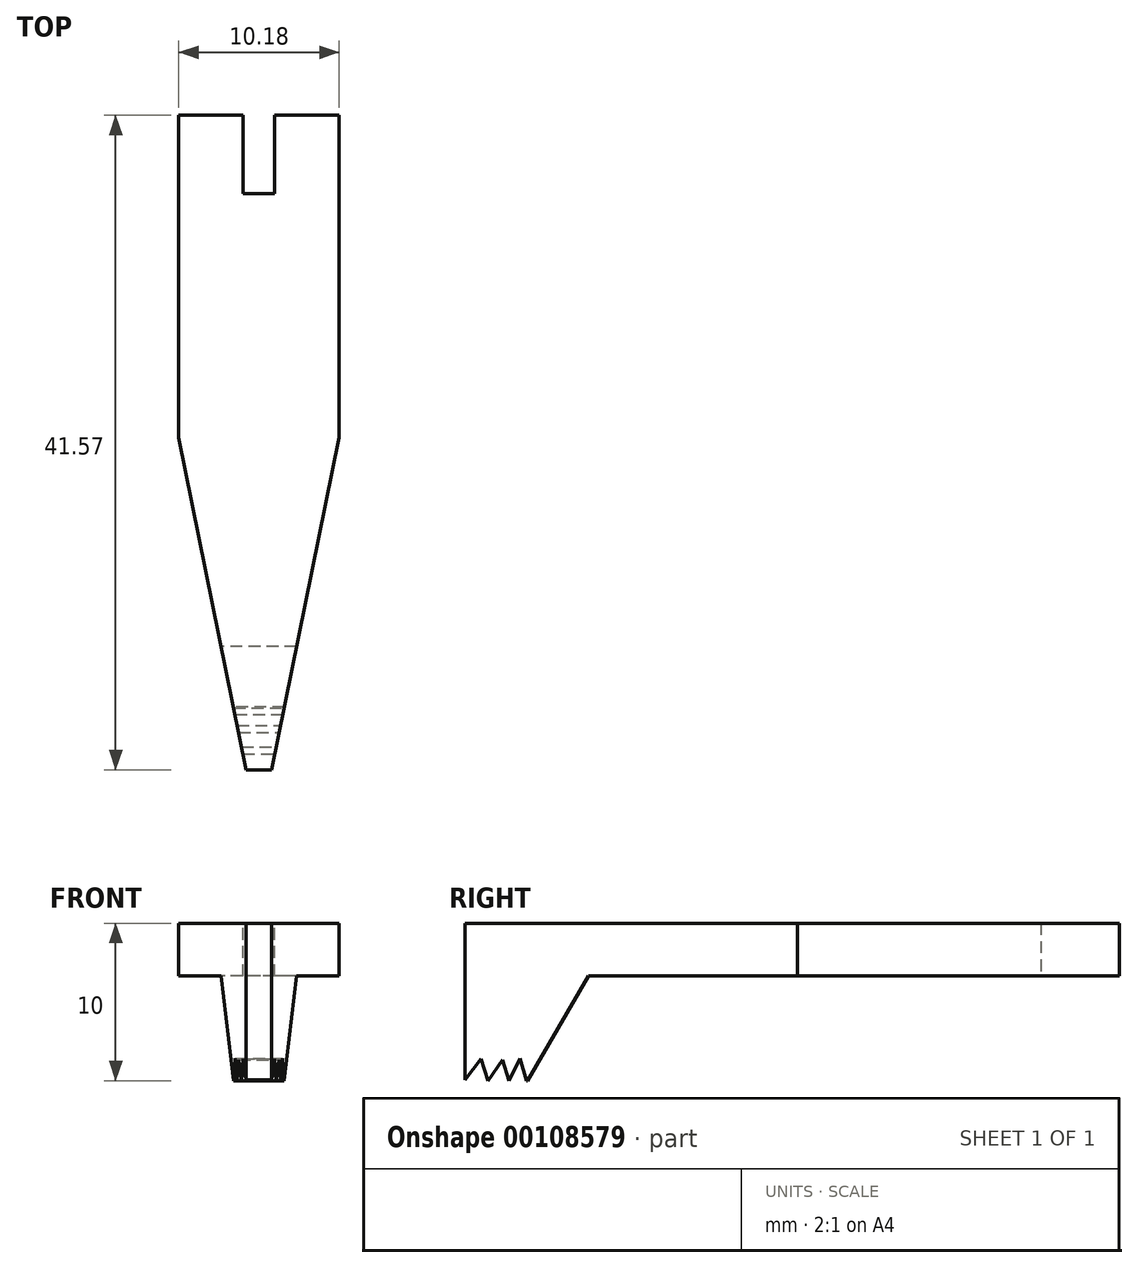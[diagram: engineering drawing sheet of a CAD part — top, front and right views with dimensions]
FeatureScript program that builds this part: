
annotation { "Feature Type Name" : "Feature", "Feature Type Description" : "" }
export const myFeature = defineFeature(function(context is Context, id is Id, definition is map)
    precondition{}
    {
        {
            var Q0;
            Q0=qCreatedBy(makeId("Top.planeOp"),FACE);
            var sketch = newSketch(context, id + "F0", { "sketchPlane" : qUnion([Q0])});
            skLineSegment(sketch, "E0", {"start": v(0, 0) * mm, "end": v(5.1, 0) * mm});
            skLineSegment(sketch, "E1", {"start": v(5.1, 0) * mm, "end": v(5.1, -20.47) * mm});
            skLineSegment(sketch, "E2", {"start": v(5.1, -20.47) * mm, "end": v(0.8, -41.57) * mm});
            skLineSegment(sketch, "E3", {"start": v(0.8, -41.57) * mm, "end": v(0, -41.57) * mm});
            skLineSegment(sketch, "E4", {"start": v(0, -41.57) * mm, "end": v(0, 0) * mm});
            skLineSegment(sketch, "E5.MirrorCS", {"start": v(0, 0) * mm, "end": v(-5.1, 0) * mm});
            skLineSegment(sketch, "E6.MirrorCS", {"start": v(-5.1, 0) * mm, "end": v(-5.1, -20.47) * mm});
            skLineSegment(sketch, "E7.MirrorCS", {"start": v(-5.1, -20.47) * mm, "end": v(-0.8, -41.57) * mm});
            skLineSegment(sketch, "E8.MirrorCS", {"start": v(-0.8, -41.57) * mm, "end": v(0, -41.57) * mm});
            skSolve(sketch);
        }
        {
            var Q0;
            Q0=makeQuery(id+"F0.imprint","IMPRINT",FACE,{"disambiguationData":[TD([[makeQuery(id+"F0.imprint","IMPRINT",EDGE,{"derivedFrom":sQuery(id+"F0.wireOp",EDGE,"E4")}),1.0]])]});
            var Q1;
            Q1=makeQuery(id+"F0.imprint","IMPRINT",FACE,{"disambiguationData":[TD([[makeQuery(id+"F0.imprint","IMPRINT",EDGE,{"derivedFrom":sQuery(id+"F0.wireOp",EDGE,"E0")}),-1.0]])]});
            extrude(context, id + "F1", {"entities" : qUnion([Q0, Q1]), "depth" : 10 * mm});
        }
        {
            var Q0;
            Q0=qCreatedBy(makeId("Right.planeOp"),FACE);
            var sketch = newSketch(context, id + "F2", { "sketchPlane" : qUnion([Q0])});
            skLineSegment(sketch, "E9", {"start": v(0, -8.96) * mm, "end": v(0, 6.65) * mm});
            skLineSegment(sketch, "E10", {"start": v(0, 6.65) * mm, "end": v(-33.74, 6.65) * mm});
            skLineSegment(sketch, "E11", {"start": v(-33.74, 6.65) * mm, "end": v(-37.6, 0) * mm});
            skLineSegment(sketch, "E12", {"start": v(-37.6, 0) * mm, "end": v(-37.6, -12.63) * mm});
            skLineSegment(sketch, "E13", {"start": v(-37.6, -12.63) * mm, "end": v(0, -8.96) * mm});
            skSolve(sketch);
        }
        {
            var Q0;
            Q0=makeQuery(id+"F2.imprint","IMPRINT",FACE,{"disambiguationData":[TD([[makeQuery(id+"F2.imprint","IMPRINT",EDGE,{"derivedFrom":sQuery(id+"F2.wireOp",EDGE,"E9")}),1.0]])]});
            extrude(context, id + "F3", {"entities" : qUnion([Q0]), "operationType" : NewBodyOperationType.REMOVE, "endBound" : BoundingType.SYMMETRIC, "depth" : 25 * mm});
        }
        {
            var Q0;
            Q0=qCreatedBy(makeId("Right.planeOp"),FACE);
            var sketch = newSketch(context, id + "F4", { "sketchPlane" : qUnion([Q0])});
            skLineSegment(sketch, "E14", {"start": v(-41.8, -0.26) * mm, "end": v(-40.56, 1.38) * mm});
            skLineSegment(sketch, "E15", {"start": v(-40.56, 1.38) * mm, "end": v(-40.1, 0) * mm});
            skLineSegment(sketch, "E16", {"start": v(-40.1, 0) * mm, "end": v(-39.2, 1.32) * mm});
            skLineSegment(sketch, "E17", {"start": v(-39.2, 1.32) * mm, "end": v(-38.77, 0) * mm});
            skLineSegment(sketch, "E18", {"start": v(-38.77, 0) * mm, "end": v(-38.07, 1.41) * mm});
            skLineSegment(sketch, "E19", {"start": v(-38.07, 1.41) * mm, "end": v(-37.65, 0) * mm});
            skLineSegment(sketch, "E20", {"start": v(-37.65, 0) * mm, "end": v(-35.92, -1.93) * mm});
            skLineSegment(sketch, "E21", {"start": v(-35.92, -1.93) * mm, "end": v(-43.11, -1.56) * mm});
            skLineSegment(sketch, "E22", {"start": v(-43.11, -1.56) * mm, "end": v(-41.8, -0.26) * mm});
            skSolve(sketch);
        }
        {
            var Q0;
            Q0=makeQuery(id+"F4.imprint","IMPRINT",FACE,{"disambiguationData":[TD([[makeQuery(id+"F4.imprint","IMPRINT",EDGE,{"derivedFrom":sQuery(id+"F4.wireOp",EDGE,"E14")}),-1.0]])]});
            extrude(context, id + "F5", {"entities" : qUnion([Q0]), "operationType" : NewBodyOperationType.REMOVE, "endBound" : BoundingType.SYMMETRIC, "oppositeDirection" : true, "depth" : 25 * mm});
        }
        {
            var Q0;
            Q0=qCreatedBy(makeId("Top.planeOp"),FACE);
            var sketch = newSketch(context, id + "F6", { "sketchPlane" : qUnion([Q0])});
            skLineSegment(sketch, "E23", {"start": v(0, 4.45) * mm, "end": v(1, 4.45) * mm});
            skLineSegment(sketch, "E24", {"start": v(1, 4.45) * mm, "end": v(1, 0) * mm});
            skLineSegment(sketch, "E25", {"start": v(1, 0) * mm, "end": v(1, -4.98) * mm});
            skLineSegment(sketch, "E26", {"start": v(1, -4.98) * mm, "end": v(0, -4.98) * mm});
            skLineSegment(sketch, "E27", {"start": v(0, -4.98) * mm, "end": v(0, 4.45) * mm});
            skLineSegment(sketch, "E28.MirrorCS", {"start": v(-1, 4.45) * mm, "end": v(-1, 0) * mm});
            skLineSegment(sketch, "E29.MirrorCS", {"start": v(0, 4.45) * mm, "end": v(-1, 4.45) * mm});
            skLineSegment(sketch, "E30.MirrorCS", {"start": v(-1, 0) * mm, "end": v(-1, -4.98) * mm});
            skLineSegment(sketch, "E31.MirrorCS", {"start": v(-1, -4.98) * mm, "end": v(0, -4.98) * mm});
            skSolve(sketch);
        }
        {
            var Q0;
            Q0=makeQuery(id+"F6.imprint","IMPRINT",FACE,{"disambiguationData":[TD([[makeQuery(id+"F6.imprint","IMPRINT",EDGE,{"derivedFrom":sQuery(id+"F6.wireOp",EDGE,"E23")}),-1.0]])]});
            var Q1;
            Q1=makeQuery(id+"F6.imprint","IMPRINT",FACE,{"disambiguationData":[TD([[makeQuery(id+"F6.imprint","IMPRINT",EDGE,{"derivedFrom":sQuery(id+"F6.wireOp",EDGE,"E27")}),1.0]])]});
            extrude(context, id + "F7", {"entities" : qUnion([Q0, Q1]), "operationType" : NewBodyOperationType.REMOVE, "depth" : 74 * mm});
        }
    });
